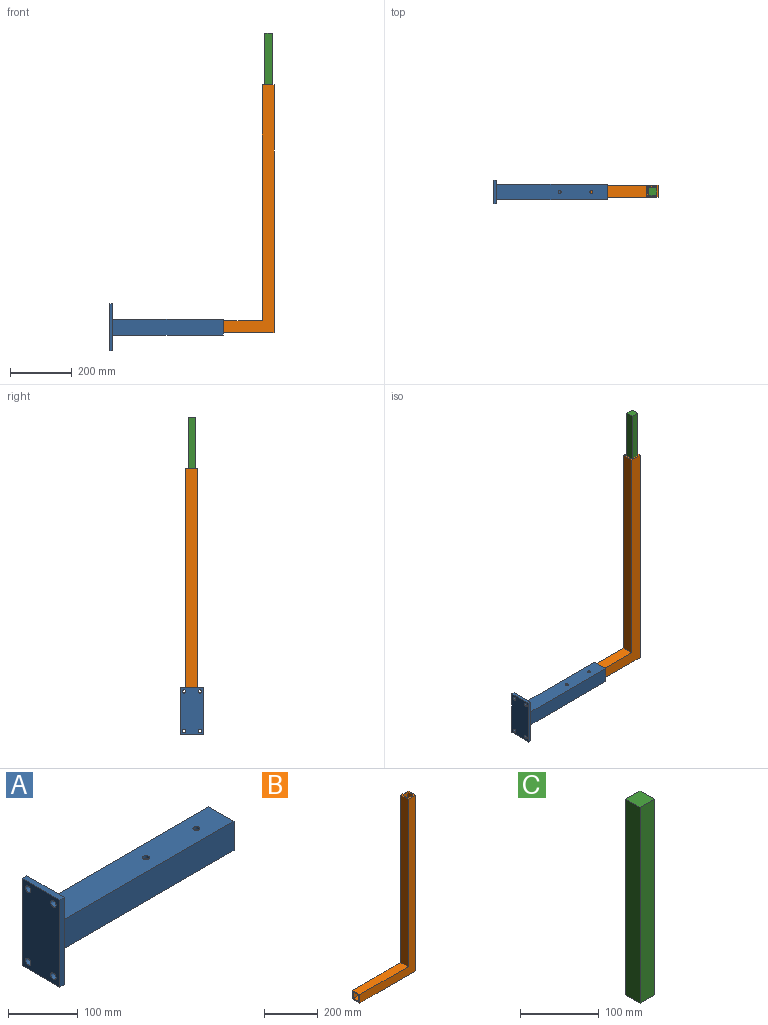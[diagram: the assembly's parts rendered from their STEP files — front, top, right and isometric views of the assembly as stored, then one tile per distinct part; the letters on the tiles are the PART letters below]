
ASSEMBLY  parts=3 mates=4
PART A: 22 faces, bbox 365.1x76.2x152.4 mm
  f0: plane 152.4x76.2mm, normal (1,0,0), area 8655.3mm2, adj f1,f2,f3,f4,f9,f10,f11,f12
  f1: plane 152.4x9.53mm, normal (0,1,0), area 1451.6mm2, adj f0,f2,f4,f5
  f2: plane 76.2x9.53mm, normal (0,0,1), area 725.8mm2, adj f0,f1,f3,f5
  f3: plane 152.4x9.53mm, normal (0,-1,0), area 1451.6mm2, adj f0,f2,f4,f5
  f4: plane 76.2x9.53mm, normal (0,0,-1), area 725.8mm2, adj f0,f1,f3,f5
  f5: plane 152.4x76.2mm, normal (-1,0,0), area 11235.9mm2, adj f1,f2,f3,f4,f16,f17,f18,f19
  f6: plane 355.6x41.28mm, normal (0,0,-1), area 14534.9mm2, adj f7,f13,f14,f15,f20,f21
  f7: plane 355.6x41.28mm, normal (0,-1,0), area 14677.4mm2, adj f6,f8,f14,f15
  f8: plane 355.6x41.28mm, normal (0,0,1), area 14677.4mm2, adj f7,f13,f14,f15
  f9: plane 355.6x50.8mm, normal (0,1,0), area 18064.5mm2, adj f0,f10,f12,f14
  f10: plane 355.6x50.8mm, normal (0,0,1), area 17922mm2, adj f0,f9,f11,f14,f20,f21
  f11: plane 355.6x50.8mm, normal (0,-1,0), area 18064.5mm2, adj f0,f10,f12,f14
  f12: plane 355.6x50.8mm, normal (0,0,-1), area 18064.5mm2, adj f0,f9,f11,f14
  f13: plane 355.6x41.28mm, normal (0,1,0), area 14677.4mm2, adj f6,f8,f14,f15
  f14: plane 50.8x50.8mm, normal (1,0,0), area 877mm2, adj f6,f7,f8,f9,f10,f11,f12,f13
  f15: plane 41.28x41.28mm, normal (1,0,0), area 1703.6mm2, adj f6,f7,f8,f13
  f16: cylinder r=5.48mm len=10.95mm, axis (1,0,0), area 327.8mm2, adj f0,f5
  f17: cylinder r=5.48mm len=10.95mm, axis (1,0,0), area 327.8mm2, adj f0,f5
  f18: cylinder r=5.48mm len=10.95mm, axis (1,0,0), area 327.8mm2, adj f0,f5
  f19: cylinder r=5.48mm len=10.95mm, axis (1,0,0), area 327.8mm2, adj f0,f5
  f20: cylinder r=4.76mm len=9.53mm, axis (0,0,1), area 142.5mm2, adj f6,f10
  f21: cylinder r=4.76mm len=9.53mm, axis (0,0,1), area 142.5mm2, adj f6,f10
PART B: 18 faces, bbox 292.1x38.1x800.1 mm
  f0: plane 38.1x38.1mm, normal (0,0,1), area 635.1mm2, adj f4,f5,f7,f8,f10,f12,f15,f16
  f1: plane 769.94x287.34mm, normal (0,-1,0), area 29395.1mm2, adj f2,f9,f10,f12,f13,f17
  f2: plane 38.1x38.1mm, normal (-1,0,0), area 635.1mm2, adj f1,f3,f6,f7,f8,f9,f13,f14
  f3: plane 292.1x38.1mm, normal (0,0,-1), area 11129mm2, adj f2,f4,f7,f8
  f4: plane 800.1x38.1mm, normal (1,0,0), area 30483.8mm2, adj f0,f3,f7,f8
  f5: plane 762x38.1mm, normal (-1,0,0), area 29032.2mm2, adj f0,f6,f7,f8
  f6: plane 254x38.1mm, normal (0,0,1), area 9677.4mm2, adj f2,f5,f7,f8
  f7: plane 800.1x292.1mm, normal (0,-1,0), area 40161.2mm2, adj f0,f2,f3,f4,f5,f6
  f8: plane 800.1x292.1mm, normal (0,1,0), area 40161.2mm2, adj f0,f2,f3,f4,f5,f6
  f9: plane 287.34x28.58mm, normal (0,0,1), area 8210.7mm2, adj f1,f2,f10,f14
  f10: plane 795.34x30.16mm, normal (-1,0,0), area 22759.5mm2, adj f0,f1,f9,f11,f14,f15,f16,f17
  f11: plane 28.58x1.59mm, normal (0,0,-1), area 45.4mm2, adj f10,f12,f14,f15
  f12: plane 766.76x30.16mm, normal (1,0,0), area 21943mm2, adj f0,f1,f11,f13,f14,f15,f16,f17
  f13: plane 258.76x28.58mm, normal (0,0,-1), area 7394.1mm2, adj f1,f2,f12,f14
  f14: plane 790.58x287.34mm, normal (0,1,0), area 29984.8mm2, adj f2,f9,f10,f11,f12,f13
  f15: plane 28.58x4.76mm, normal (0,1,0), area 136.1mm2, adj f0,f10,f11,f12
  f16: plane 28.58x25.4mm, normal (0,-1,0), area 725.8mm2, adj f0,f10,f12,f17
  f17: plane 28.58x1.59mm, normal (0,0,1), area 45.4mm2, adj f1,f10,f12,f16
PART C: 6 faces, bbox 25.4x25.4x304.8 mm
  f0: plane 304.8x25.4mm, normal (1,0,0), area 7741.9mm2, adj f1,f3,f4,f5
  f1: plane 304.8x25.4mm, normal (0,1,0), area 7741.9mm2, adj f0,f2,f4,f5
  f2: plane 304.8x25.4mm, normal (-1,0,0), area 7741.9mm2, adj f1,f3,f4,f5
  f3: plane 304.8x25.4mm, normal (0,-1,0), area 7741.9mm2, adj f0,f2,f4,f5
  f4: plane 25.4x25.4mm, normal (0,0,1), area 645.2mm2, adj f0,f1,f2,f3
  f5: plane 25.4x25.4mm, normal (0,0,-1), area 645.2mm2, adj f0,f1,f2,f3
PLACE A t=(-100.82,-76.99,-988.86)mm
PLACE B t=(136.73,-56.36,-1006.32)mm
PLACE C t=(411.37,-76.99,-344.57)mm
MATE planar A.f6 <-> B.f6  axis (0,0,-1) through (264.3,-76.99,-968.22)mm
MATE planar B.f8 <-> A.f7  axis (0,1,0) through (282.78,-56.36,-1006.32)mm
MATE planar C.f3 <-> B.f14  axis (0,-1,0) through (398.67,-89.69,-192.17)mm
MATE planar B.f10 <-> C.f0  axis (-1,0,0) through (424.07,-75.37,-603.34)mm
